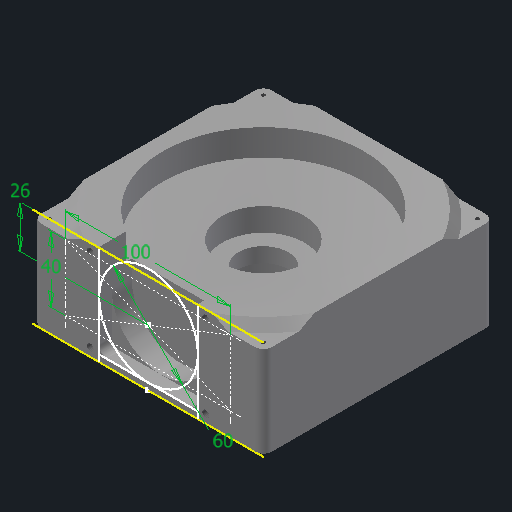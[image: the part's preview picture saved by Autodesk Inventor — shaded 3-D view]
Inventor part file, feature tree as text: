
AUTODESK INVENTOR PART (.ipt)
format: ipt  version: 2022 (Build 260153000, 153)  size: 279,552 bytes
history: native  units: mm
features: sketch x11, extrude x9, reference x6, plane x3, other x3, fillet x2, hole x2, projected_geometry x2, chamfer x1
ambient origin geometry x8: Origin, YZ Plane, XZ Plane, XY Plane, X Axis, Y Axis, Z Axis, Center Point
bodies: Body1 (feature_tree)
feature tree (39):
  extrude  "Extrusion10"  Depth=30.0mm
  plane  "Work Plane6"
  extrude  "Extrusion11"  Depth=140.0mm
  sketch  "Sketch15"  dims[d79=60.0mm d80=0.0mm d81=50.0mm]
  extrude  "Extrusion19"  Depth=50.0mm
  plane  "Work Plane5"
  plane  "Work Plane7"
  sketch  "Sketch17"  dims[d82=30.0mm d83=0.0mm d140=100.0mm]
  extrude  "Extrusion23"  Depth=100.0mm
  extrude  "Extrusion24"  Depth=40.0mm
  fillet  "Fillet5"  Radius=20.0mm
  hole  "Hole4"  [1 undecoded]
  extrude  "Extrusion25"  Depth=8.0mm TaperAngle=0.0deg
  chamfer  "Chamfer6"  Distance=8.0mm
  hole  "Hole5"  [1 undecoded]
  fillet  "Fillet6"  Radius=130.0mm
  extrude  "Extrusion26"  Depth=5.0mm
  extrude  "Extrusion27"  Depth=5.0mm TaperAngle=0.0deg
  extrude  "Extrusion28"  Depth=5.0mm TaperAngle=45.0deg
  sketch  "Sketch8"  dims[d71=200.0mm d72=30.0mm]
  sketch  "Sketch9"  dims[d73=140.0mm d74=70.0mm]
  sketch  "Sketch20"  dims[d141=40.0mm d143=60.0mm d145=20.0mm d146=0.0mm]
  sketch  "Sketch21"  dims[d151=26.0mm d152=70.0mm]
  reference  "Reference2"
  reference  "Reference3"
  reference  "Reference4"
  reference  "Reference5"
  sketch  "Sketch22"  dims[d158=122.0mm d159=16.0mm d160=0.0mm d162=8.0mm d163=0.0mm]
  projected_geometry  "Projected Loop8"
  sketch  "Sketch23"  dims[d164=5.0mm]
  projected_geometry  "Projected Loop9"
  sketch  "Sketch24"  dims[d165=4.134mm d166=10.0mm d167=10.4mm d168=2.0mm d169=90.0deg d170=14.2mm d171=20.594885mm d172=130.0mm d173=130.0mm]
  sketch  "Sketch25"  dims[d174=2.459mm d175=6.0mm d176=4.0mm d177=2.0mm d178=90.0deg d179=8.8mm d180=20.594885mm d181=5.0mm]
  reference  "Reference6"
  reference  "Reference7"
  sketch  "Sketch26"  dims[d182=170.0mm d183=5.0mm d184=0.0mm d185=5.0mm d186=2.0mm d187=45.0deg d188=52.0mm d189=21.0mm d190=0.0mm d191=8.0mm d192=0.0mm d193=2.0mm d194=0.5mm d195=0.0mm d8=0.5mm d9=0.872665mm d10=0.5mm d11=0.872665mm d25=0.5mm d26=0.872665mm d27=0.5mm d28=0.872665mm d33=0.5mm d34=0.872665mm d35=0.5mm d36=0.872665mm d61=0.5mm d62=0.872665mm d63=0.5mm d64=0.872665mm d123=0.0mm d124=0.0mm d125=0.0mm d126=0.0mm d127=0.0mm d128=0.0mm d129=0.0mm d153=0.872665mm d154=0.5mm d155=0.872665mm d161=0.0mm]
  other  "SistemaDeElevación.iam"
  other  "Montura de Motor:1"
  other  "Brida de rodamientos:1"
note: 2 required parameter values undecoded (feature->parameter linkage not recoverable at this tier; creation-order binding heuristic only, values carry confidence <= 0.55)
